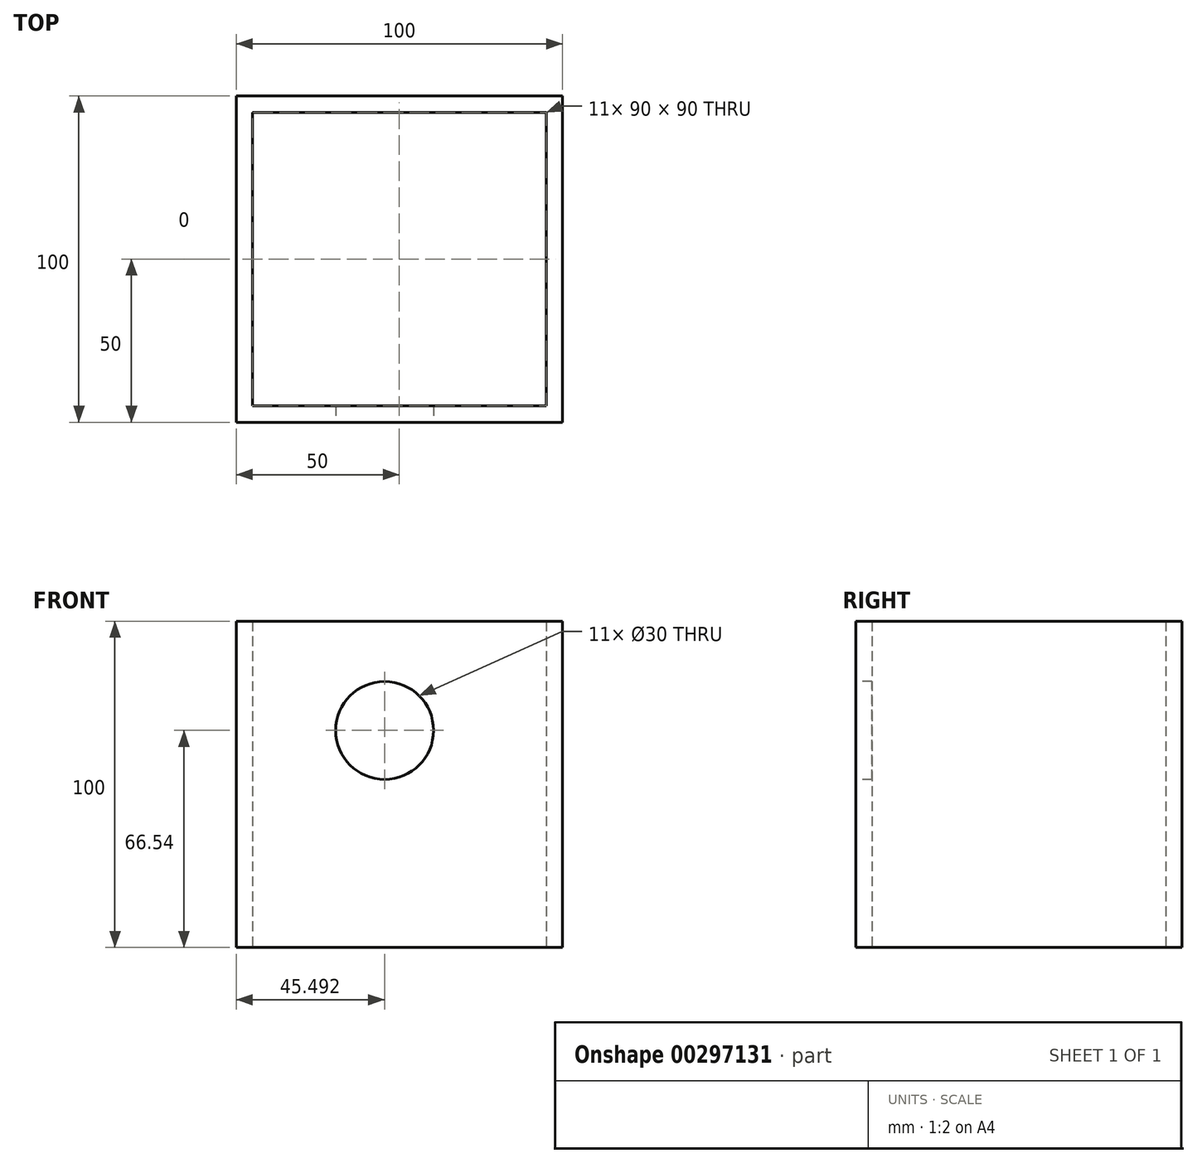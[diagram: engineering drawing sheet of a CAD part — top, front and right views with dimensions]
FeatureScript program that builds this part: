
annotation { "Feature Type Name" : "Feature", "Feature Type Description" : "" }
export const myFeature = defineFeature(function(context is Context, id is Id, definition is map)
    precondition{}
    {
        {
            var Q0;
            Q0=qCreatedBy(makeId("Top.planeOp"),FACE);
            var sketch = newSketch(context, id + "F0", { "sketchPlane" : qUnion([Q0])});
            skLineSegment(sketch, "E0.bottom", {"start": v(50, 50) * mm, "end": v(-50, 50) * mm});
            skLineSegment(sketch, "E0.top", {"start": v(50, -50) * mm, "end": v(-50, -50) * mm});
            skLineSegment(sketch, "E0.left", {"start": v(50, 50) * mm, "end": v(50, -50) * mm});
            skLineSegment(sketch, "E0.right", {"start": v(-50, 50) * mm, "end": v(-50, -50) * mm});
            skPoint(sketch, "E0.middle", {"position": v(0, 0) * mm});
            skLineSegment(sketch, "E1.bottom", {"start": v(45, 45) * mm, "end": v(-45, 45) * mm});
            skLineSegment(sketch, "E1.top", {"start": v(45, -45) * mm, "end": v(-45, -45) * mm});
            skLineSegment(sketch, "E1.left", {"start": v(45, 45) * mm, "end": v(45, -45) * mm});
            skLineSegment(sketch, "E1.right", {"start": v(-45, 45) * mm, "end": v(-45, -45) * mm});
            skSolve(sketch);
        }
        {
            var Q0;
            Q0=makeQuery(id+"F0.imprint","IMPRINT",FACE,{"disambiguationData":[TD([[makeQuery(id+"F0.imprint","IMPRINT",EDGE,{"derivedFrom":sQuery(id+"F0.wireOp",EDGE,"E0.bottom")}),1.0]])]});
            extrude(context, id + "F1", {"entities" : qUnion([Q0]), "depth" : 100 * mm});
        }
        {
            var Q0;
            Q0=makeQuery(id+"F1.opExtrude","SWEPT_FACE",FACE,{"disambiguationData":[OSD([sQuery(id+"F0.wireOp",EDGE,"E0.top")])]});
            var sketch = newSketch(context, id + "F2", { "sketchPlane" : qUnion([Q0])});
            skCircle(sketch, "E2", {"center": v(-4.89, 68.33) * mm, "radius": 15 * mm});
            skSolve(sketch);
        }
        {
            var Q0;
            Q0=makeQuery(id+"F2.imprint","IMPRINT",FACE,{"disambiguationData":[TD([[makeQuery(id+"F2.imprint","IMPRINT",EDGE,{"derivedFrom":sQuery(id+"F2.wireOp",EDGE,"E2")}),1.0]])]});
            extrude(context, id + "F3", {"entities" : qUnion([Q0]), "operationType" : NewBodyOperationType.REMOVE, "depth" : 10 * mm});
        }
        {
            var Q0;
            Q0=makeQuery(id+"F1.opExtrude","SWEPT_FACE",FACE,{"disambiguationData":[OSD([sQuery(id+"F0.wireOp",EDGE,"E0.top")])]});
            var sketch = newSketch(context, id + "F4", { "sketchPlane" : qUnion([Q0])});
            skCircle(sketch, "E3", {"center": v(-4.5, 66.54) * mm, "radius": 15 * mm});
            skSolve(sketch);
        }
        {
            var Q0;
            Q0 = qSketchRegion(id + "F4", true);
            var Q1;
            Q1=makeQuery(id+"F4.imprint","IMPRINT",FACE,{"disambiguationData":[TD([[makeQuery(id+"F4.imprint","IMPRINT",EDGE,{"derivedFrom":sQuery(id+"F4.wireOp",EDGE,"E3")}),1.0]])]});
            extrude(context, id + "F5", {"entities" : qUnion([Q0, Q1]), "operationType" : NewBodyOperationType.REMOVE, "oppositeDirection" : true, "depth" : 25 * mm});
        }
    });
